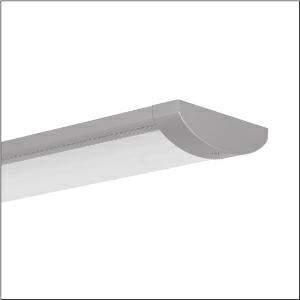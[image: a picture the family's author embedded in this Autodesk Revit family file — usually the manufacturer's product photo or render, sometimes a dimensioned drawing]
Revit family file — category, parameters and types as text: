
# Revit family: tv_20_5xa86174n0x
name_source: partatom
category: Lighting Fixtures
units: mm (PartAtom-declared; Revit-internal decimal feet)

## family parameters
Cut with Voids When Loaded = No
Host = Face
Light Source = No
Part Type = Normal
Room Calculation Point = No
Round Connector Dimension = Use Diameter
Shared = No

## types (1)
- TV 20 (1 x LED 4000K / CRI = 80 (unbekannt), 5120 lm, 4000K)
    Apparent Load = 50 VA
    CIE Flux Codes = 48 78 95 99 100
    Color Rendering = 80
    Color Temperature = 4000K
    Default Elevation = 1800 mm
    Description = TV 20, vandal-proof luminaire, primary light control with specular reflector, of aluminium, matt, primary optical cover: enclosure, of PC, frosted, light emission: direct distribution, primary light characteristic: symmetric, installation type: surface-mounted, LED, rated luminous flux: 5.120lm, luminous efficacy: 102lm/W, light colour: 840, colour temperature: 4000K, control gear: ON/OFF, mains connection: 230V, AC, 50Hz, rated input power: 50W, luminaire housing, of aluminium, coated, SITECO metallic grey (DB 702S), with wall and ceiling fixing element, length: 1.561mm, width: 260mm, height: 70mm, mounting height: 2.5..4.0m, protection rating (complete): IP65, insulation class (complete): insulation class I (protective earthing), certification: CE, protection symbol: F, impact resistance: 2x IK10, standard: EN 60598, packaging unit: 1 piece
    Height = 70 mm
    Lamp = 1 x LED 4000K / CRI >= 80 (unbekannt)
    Lamp Light Flux = 5120 lm
    Lamp count = 1
    Length = 1561 mm
    Luminous efficacy = 102 lm/W
    Manufacturer = Siteco
    ModVariant = No
    Model = 5XA86174N0X
    Mounting Place = Ceiling
    Mounting Type = Surface mounted
    Number of Poles = 1
    OnlyDefault = Yes
    Power Factor = 1
    Product Name = TV 20
    Product group = vandal-proof luminaire
    ProductGroupID = 310
    Protection Class = Protection class I
    Protection Degree = IP 65
    RLX_Detail_Level = 1
    RLX_Emergency_Light_Flux = 0 lm
    RLX_Emergency_Type = 0
    RLX_Emergency_Type_DB = No
    RlxData = <blob elided: 25301 chars, md5=43183197>
    Socket = socket
    Standby Power = 0 W
    System Light Flux = 5120 lm
    System Power = 50 W
    Type Comments = Product without accessories
    Type Image = l_1004809.jpg
    URL = http://relux.com
    VarID = ---
    Voltage = 0 V
    Weight = 0.00 kg
    Width = 260 mm

## geometry (parser evidence)
native form markers: Blend x4, Sweep x12
no freeform markers — native parametric forms only
